# Revit family: MTXTYP006
name_source: partatom
category: Furniture
units: mm (PartAtom-declared; Revit-internal decimal feet)

## family parameters
Always vertical = Yes
Cut with Voids When Loaded = No
OmniClass Number = 23.40.20.00
OmniClass Title = General Furniture and Specialties
Render Appearance Source = Family Geometry
Room Calculation Point = No
Shared = No
Work Plane-Based = No

## types (1)
- MTXTYP006
    Cost = 53936 $
    Default Elevation = 0 mm  [stored 0 ft]
    Description = 2 x Overhead - Shared - Laminated 16H X 36W X 16D, 1 x 63 in. Electrical Jumper  (Pt 42E), 2 x Matrix Black Duplex Outlet - Line 1, 2 x Matrix Black Duplex Outlet - Line 2, 2 x Matrix Black Duplex Outlet - Line 3, 2 x Matrix Black Duplex Outlet - Line 4 - Dedicated, 1 x 18 in. Electrical Jumper  (Panel To Panel), 4 x 21 in. Electrical Jumper  (Extended Panel To Panel), 2 x Single Powerway Assembly - 30W - 8 wire, 4 circuit, 2 x Single Powerway Assembly - 42W - 8 wire, 4 circuit, 4 x Double Powerway Assembly - 42W - 8 wire, 4 circuit, 1 x RH Receptacle Mounted Base Infeed - 72L - 8 Wire, 4 Circuit, 1 x 24 in. Electrical Jumper  (Vt 24), 1 x Dual Electrical Tile - 8H X 42W, 4 x Quad Electrical Tile - 8H X 42W, 4 x Laminate Tile - 16H x 30W, 17 x Laminate Tile - 16H x 42W, 4 x MX Monolithic Laminate Tile Single Sided 24H X 30W, 7 x MX Monolithic Laminate Tile Single Sided 24H X 42W, 2 x 3-Way  90 Degree Connector - Linear Trim - 42H, 1 x MATRIX LINEAR Double Frame Recessed Glass Kit 30" & 42", 4 x Frame End Cap - Linear Trim - 42H, 2 x Panel Frame - Linear Trim - 42H x 30W, 6 x Panel Frame - Linear Trim - 42H x 42W, 1 x MATRIX RECESSED FRAMELESS GLASS 8"H X 72"W V2, 8 x MTX Double Sided Monolithic Laminate Tile Mounting Kit, 4 x Rectangular - 2mm Edge - 30D x 72W, 4 x Post Leg 2.5 x 2.5 27H, 4 x Side/Support Rear Bracket - Left, 4 x Side/Support Rear Bracket - Right, 2 x Regular Cantilever - Left Hand - 30D, 2 x Regular Cantilever - Right Hand - 30D, 2 x CBX Combo B/F Ped Left/Bookcase Right 18D x 21H x 72W, 2 x CBX Combo B/F Ped Right/Bookcase Left 18D x 21H x 72W
    Exported From CET Designer = Yes
    Manufacturer = AIS
    Model = C-SOLMX163616
    Show MTXTYP006 = Yes
    VisibilityIndex = 0

note: [stored X ft] marks values corroborated as IEEE doubles in the binary element streams (Revit-internal decimal feet)

## geometry (parser evidence)
native form markers: Sweep x3
no freeform markers — native parametric forms only
